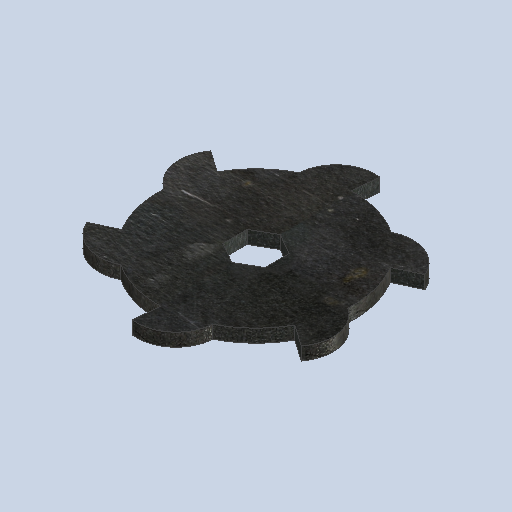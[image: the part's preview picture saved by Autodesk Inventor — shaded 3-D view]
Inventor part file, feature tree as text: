
AUTODESK INVENTOR PART (.ipt)
format: ipt  version: 2025 (Build 290162010, 162A)  size: 260,096 bytes
history: native  units: mm
features: extrude x2, sketch x2, pattern_circular x1, other x1
ambient origin geometry x8: Origin, YZ Plane, XZ Plane, XY Plane, X Axis, Y Axis, Z Axis, Center Point
bodies: Solid1 (feature_tree)
feature tree (6):
  extrude  "Extrusion1"  Depth=32.2mm
  extrude  "Extrusion2"  Depth=10.0mm TaperAngle=0.0deg
  pattern_circular  "Circular Pattern1"  [2 undecoded]
  sketch  "Sketch1"  dims[d0=32.2mm d1=200.0mm]
  sketch  "Sketch2"  dims[d2=150.0mm d3=10.0mm d4=0.0mm d5=0.872665mm d8=6.108652mm d9=10.0mm d10=0.0mm d11=60.0mm d12=360.0deg d14=30.0deg d15=30.0mm d16=33.0mm d17=20.0mm]
  other  "Definition1"
note: 2 required parameter values undecoded (feature->parameter linkage not recoverable at this tier; creation-order binding heuristic only, values carry confidence <= 0.55)
